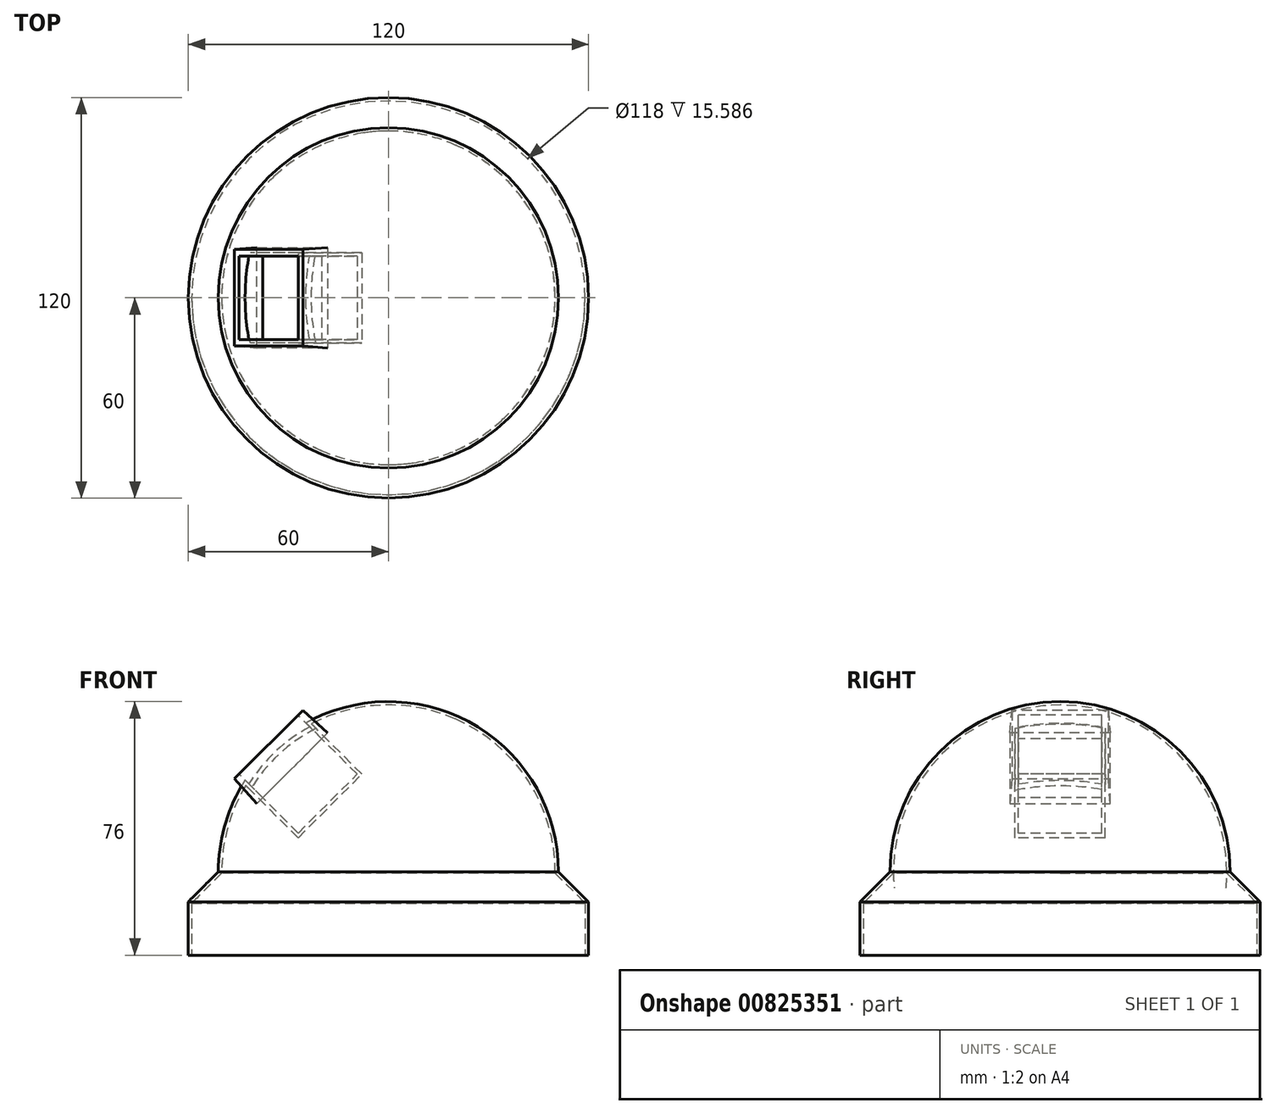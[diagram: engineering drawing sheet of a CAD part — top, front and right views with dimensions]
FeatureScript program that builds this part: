
annotation { "Feature Type Name" : "Feature", "Feature Type Description" : "" }
export const myFeature = defineFeature(function(context is Context, id is Id, definition is map)
    precondition{}
    {
        {
            var Q0;
            Q0=qCreatedBy(makeId("Top.planeOp"),FACE);
            var sketch = newSketch(context, id + "F0", { "sketchPlane" : qUnion([Q0])});
            skCircle(sketch, "E0", {"center": v(0, 0) * mm, "radius": 60 * mm});
            skSolve(sketch);
        }
        {
            var Q0;
            Q0=makeQuery(id+"F0.imprint","IMPRINT",FACE,{"disambiguationData":[TD([[makeQuery(id+"F0.imprint","IMPRINT",EDGE,{"derivedFrom":sQuery(id+"F0.wireOp",EDGE,"E0")}),1.0]])]});
            extrude(context, id + "F1", {"entities" : qUnion([Q0]), "depth" : 25 * mm, "offsetDistance" : 25 * mm});
        }
        {
            var Q0;
            Q0=makeQuery(id+"F1.opExtrude","CAP_FACE",FACE,{"disambiguationData":[OSD([sQuery(id+"F0.wireOp",EDGE,"E0")])],"isStart":false});
            var sketch = newSketch(context, id + "F2", { "sketchPlane" : qUnion([Q0])});
            skLineSegment(sketch, "E1", {"start": v(0, 51) * mm, "end": v(0, -51) * mm});
            skArc(sketch, "E2", {"start": v(0, 51) * mm, "mid": v(-51, 0) * mm, "end": v(0, -51) * mm});
            skPoint(sketch, "E3.orphan", {"position": v(0, 60) * mm});
            skSolve(sketch);
        }
        {
            var Q0;
            Q0=makeQuery(id+"F2.imprint","IMPRINT",FACE,{"disambiguationData":[TD([[makeQuery(id+"F2.imprint","IMPRINT",EDGE,{"derivedFrom":sQuery(id+"F2.wireOp",EDGE,"E1")}),-1.0]])]});
            var Q1;
            Q1=sQuery(id+"F2.wireOp",EDGE,"E1");
            revolve(context, id + "F3", {"operationType" : NewBodyOperationType.ADD, "surfaceOperationType" : NewSurfaceOperationType.NEW, "entities" : qUnion([Q0]), "axis" : qUnion([Q1]), "revolveType" : RevolveType.ONE_DIRECTION, "oppositeDirection" : true, "angle" : 180 * degree});
        }
        {
            var Q0;
            Q0=makeQuery(id+"F1.opExtrude","CAP_EDGE",EDGE,{"disambiguationData":[OSD([sQuery(id+"F0.wireOp",EDGE,"E0")])],"isStart":false});
            chamfer(context, id + "F4", {"entities" : qUnion([Q0]), "chamferType" : ChamferType.TWO_OFFSETS, "width1" : 9 * mm, "oppositeDirection" : false, "width2" : 9 * mm, "tangentPropagation" : true});
        }
        {
            var Q0;
            Q0=qCreatedBy(makeId("Top.planeOp"),FACE);
            var Q1;
            Q1=qCreatedBy(makeId("Right.planeOp"),FACE);
            cPlane(context, id + "F5", {"entities" : qUnion([Q0, Q1]), "cplaneType" : CPlaneType.MID_PLANE, "offset" : 25 * mm, "width" : 150 * mm, "height" : 150 * mm});
        }
        {
            var Q0;
            Q0=qCreatedBy(id+"F5.planeOp",FACE);
            cPlane(context, id + "F6", {"entities" : qUnion([Q0]), "cplaneType" : CPlaneType.OFFSET, "offset" : 60 * mm, "width" : 150 * mm, "height" : 150 * mm});
        }
        {
            var Q0;
            Q0=qCreatedBy(id+"F6.planeOp",FACE);
            var sketch = newSketch(context, id + "F7", { "sketchPlane" : qUnion([Q0])});
            skLineSegment(sketch, "E4.bottom", {"start": v(-15, 4.22) * mm, "end": v(15, 4.22) * mm});
            skLineSegment(sketch, "E4.top", {"start": v(-15, 34.22) * mm, "end": v(15, 34.22) * mm});
            skLineSegment(sketch, "E4.left", {"start": v(-15, 4.22) * mm, "end": v(-15, 34.22) * mm});
            skLineSegment(sketch, "E4.right", {"start": v(15, 4.22) * mm, "end": v(15, 34.22) * mm});
            skPoint(sketch, "E4.middle", {"position": v(0, 19.22) * mm});
            skSolve(sketch);
        }
        {
            var Q0;
            Q0 = qSketchRegion(id + "F7", true);
            extrude(context, id + "F8", {"entities" : qUnion([Q0]), "depth" : 10 * mm, "offsetDistance" : 25 * mm, "hasDraft" : true, "draftAngle" : 3 * degree, "draftPullDirection" : true});
        }
        {
            var Q0;
            Q0=makeQuery(id+"F8.opExtrude","CAP_FACE",FACE,{"disambiguationData":[OSD([sQuery(id+"F7.wireOp",EDGE,"E4.bottom"),sQuery(id+"F7.wireOp",EDGE,"E4.top"),sQuery(id+"F7.wireOp",EDGE,"E4.left"),sQuery(id+"F7.wireOp",EDGE,"E4.right")])],"isStart":false});
            var sketch = newSketch(context, id + "F9", { "sketchPlane" : qUnion([Q0])});
            skLineSegment(sketch, "E5.bottom", {"start": v(-12.5, 6.72) * mm, "end": v(12.5, 6.72) * mm});
            skLineSegment(sketch, "E5.top", {"start": v(-12.5, 31.72) * mm, "end": v(12.5, 31.72) * mm});
            skLineSegment(sketch, "E5.left", {"start": v(-12.5, 6.72) * mm, "end": v(-12.5, 31.72) * mm});
            skLineSegment(sketch, "E5.right", {"start": v(12.5, 6.72) * mm, "end": v(12.5, 31.72) * mm});
            skPoint(sketch, "E5.middle", {"position": v(0, 19.22) * mm});
            skPoint(sketch, "E5.middle.positionSnap0", {"position": v(-14.48, 19.22) * mm});
            skPoint(sketch, "E5.middle.positionSnap1", {"position": v(0, 33.7) * mm});
            skPoint(sketch, "E5.centerSnap0", {"position": v(-14.48, 19.22) * mm});
            skPoint(sketch, "E5.centerSnap1", {"position": v(0, 33.7) * mm});
            skSolve(sketch);
        }
        {
            var Q0;
            Q0=makeQuery(id+"F9.imprint","IMPRINT",FACE,{"disambiguationData":[TD([[makeQuery(id+"F9.imprint","IMPRINT",EDGE,{"derivedFrom":sQuery(id+"F9.wireOp",EDGE,"E5.bottom")}),1.0]])]});
            extrude(context, id + "F10", {"entities" : qUnion([Q0]), "operationType" : NewBodyOperationType.REMOVE, "oppositeDirection" : true, "depth" : 25 * mm, "offsetDistance" : 25 * mm});
        }
        {
            var Q0;
            Q0=makeQuery(id+"F1.opExtrude","CAP_FACE",FACE,{"disambiguationData":[OSD([sQuery(id+"F0.wireOp",EDGE,"E0")])],"isStart":true});
            shell(context, id + "F11", {"entities" : qUnion([Q0]), "thickness" : 1 * mm});
        }
    });
